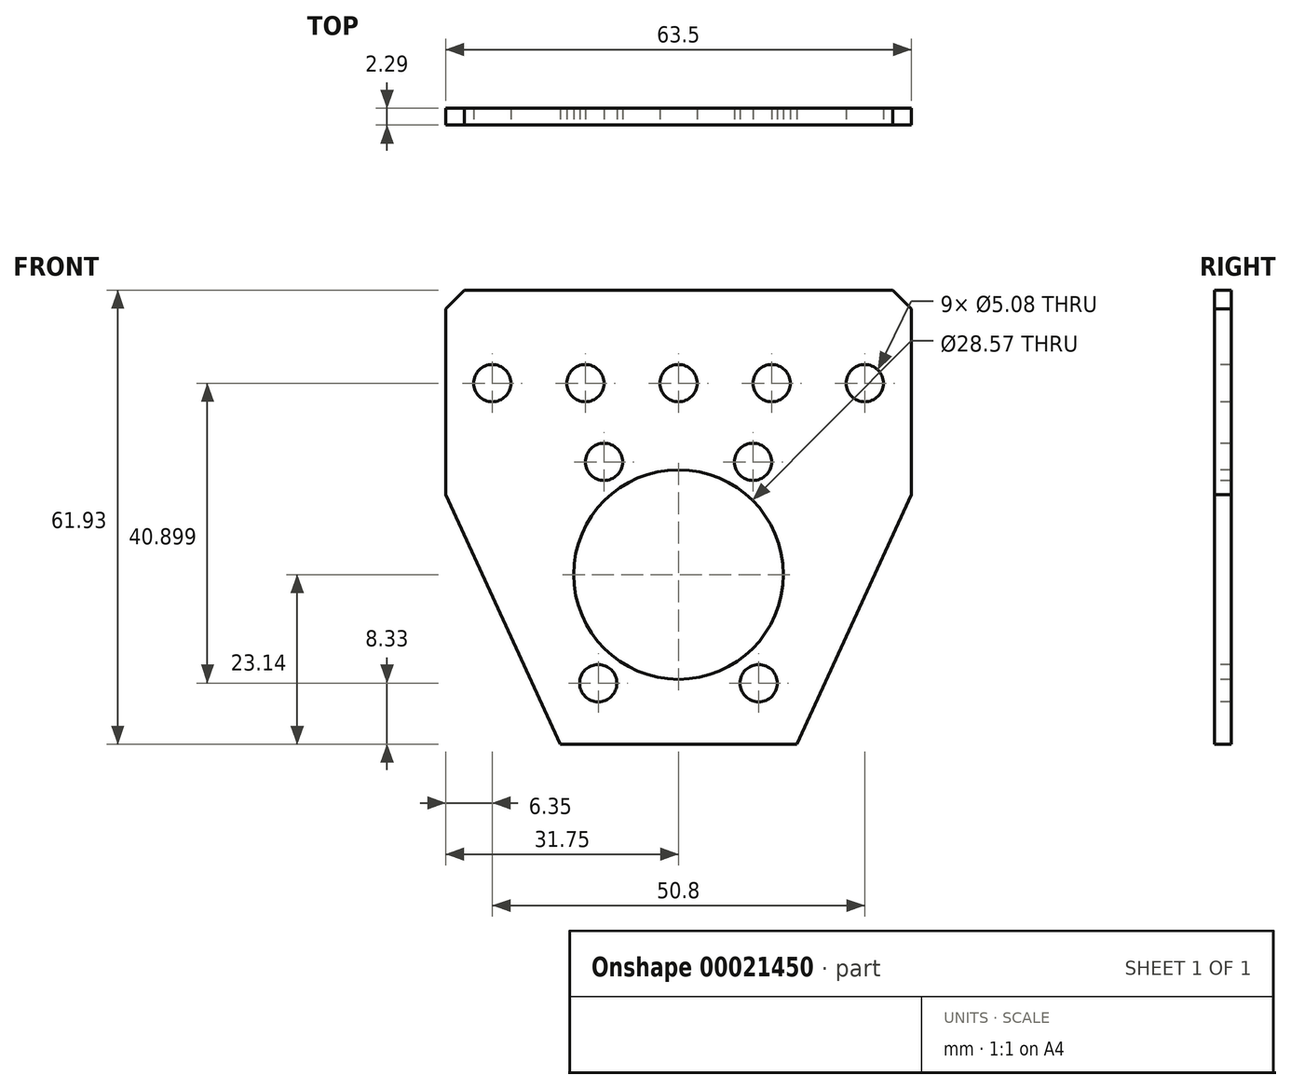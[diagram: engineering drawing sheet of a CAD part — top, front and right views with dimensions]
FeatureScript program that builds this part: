
annotation { "Feature Type Name" : "Feature", "Feature Type Description" : "" }
export const myFeature = defineFeature(function(context is Context, id is Id, definition is map)
    precondition{}
    {
        {
            var Q0;
            Q0=qCreatedBy(makeId("Front.planeOp"),FACE);
            var sketch = newSketch(context, id + "F0", { "sketchPlane" : qUnion([Q0])});
            skLineSegment(sketch, "E0.rect.bottom", {"start": v(-31.75, 38.79) * mm, "end": v(31.75, 38.79) * mm});
            skLineSegment(sketch, "E0.rect.top", {"start": v(-16.1, -23.14) * mm, "end": v(16.1, -23.14) * mm});
            skLineSegment(sketch, "E0.rect.left", {"start": v(-31.75, 38.79) * mm, "end": v(-31.75, 10.89) * mm});
            skLineSegment(sketch, "E0.rect.right", {"start": v(31.75, 38.79) * mm, "end": v(31.75, 10.89) * mm});
            skPoint(sketch, "E0.rect.middle", {"position": v(0, 0) * mm});
            skLineSegment(sketch, "E1", {"start": v(0, -23.14) * mm, "end": v(0, 38.79) * mm, "construction": true});
            skLineSegment(sketch, "E2", {"start": v(-31.75, 10.89) * mm, "end": v(-16.1, -23.14) * mm});
            skLineSegment(sketch, "E3", {"start": v(31.75, 10.89) * mm, "end": v(16.1, -23.14) * mm});
            skCircle(sketch, "E4", {"center": v(0, 0) * mm, "radius": 14.29 * mm});
            skLineSegment(sketch, "E5", {"start": v(-14.29, 0) * mm, "end": v(14.29, 0) * mm, "construction": true});
            skLineSegment(sketch, "E6", {"start": v(-31.75, 26.09) * mm, "end": v(31.75, 26.09) * mm, "construction": true});
            skLineSegment(sketch, "E7", {"start": v(-25.4, 38.79) * mm, "end": v(-25.4, 26.09) * mm, "construction": true});
            skLineSegment(sketch, "E8", {"start": v(25.4, 38.79) * mm, "end": v(25.4, 26.09) * mm, "construction": true});
            skLineSegment(sketch, "E9", {"start": v(12.7, 38.79) * mm, "end": v(12.7, 26.09) * mm, "construction": true});
            skLineSegment(sketch, "E10", {"start": v(-12.7, 38.79) * mm, "end": v(-12.7, 26.09) * mm, "construction": true});
            skCircle(sketch, "E11", {"center": v(-25.4, 26.09) * mm, "radius": 2.54 * mm});
            skCircle(sketch, "E12", {"center": v(-12.7, 26.09) * mm, "radius": 2.54 * mm});
            skCircle(sketch, "E13", {"center": v(0, 26.09) * mm, "radius": 2.54 * mm});
            skCircle(sketch, "E14", {"center": v(12.7, 26.09) * mm, "radius": 2.54 * mm});
            skCircle(sketch, "E15", {"center": v(25.4, 26.09) * mm, "radius": 2.54 * mm});
            skCircle(sketch, "E16", {"center": v(0, 0) * mm, "radius": 18.41 * mm, "construction": true});
            skCircle(sketch, "E17", {"center": v(-10.94, -14.81) * mm, "radius": 2.54 * mm});
            skCircle(sketch, "E18", {"center": v(10.94, -14.81) * mm, "radius": 2.54 * mm});
            skCircle(sketch, "E19", {"center": v(10.16, 15.36) * mm, "radius": 2.54 * mm});
            skCircle(sketch, "E20", {"center": v(-10.16, 15.36) * mm, "radius": 2.54 * mm});
            skSolve(sketch);
        }
        {
            var Q0;
            Q0=makeQuery(id+"F0.imprint","IMPRINT",FACE,{"disambiguationData":[TD([[makeQuery(id+"F0.imprint","IMPRINT",EDGE,{"derivedFrom":sQuery(id+"F0.wireOp",EDGE,"E0.rect.bottom")}),-1.0]])]});
            extrude(context, id + "F1", {"entities" : qUnion([Q0]), "oppositeDirection" : true, "depth" : 2.3 * mm});
        }
        {
            var Q0;
            Q0=makeQuery(id+"F1.opExtrude","SWEPT_EDGE",EDGE,{"disambiguationData":[OSD([sQuery(id+"F0.wireOp",EDGE,"E0.rect.bottom"),sQuery(id+"F0.wireOp",EDGE,"E0.rect.left")])]});
            var Q1;
            Q1=makeQuery(id+"F1.opExtrude","SWEPT_EDGE",EDGE,{"disambiguationData":[OSD([sQuery(id+"F0.wireOp",EDGE,"E0.rect.bottom"),sQuery(id+"F0.wireOp",EDGE,"E0.rect.right")])]});
            chamfer(context, id + "F2", {"entities" : qUnion([Q0, Q1]), "width" : 2.54 * mm, "tangentPropagation" : true});
        }
    });
